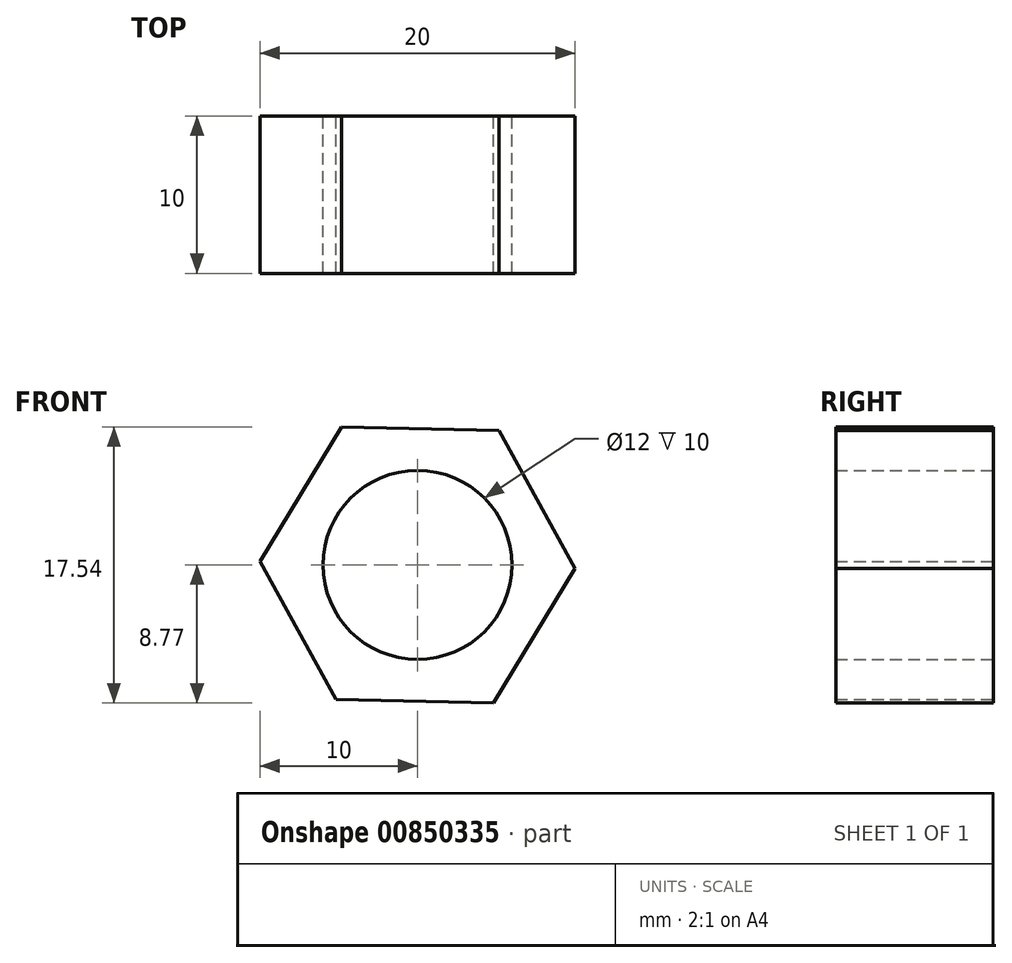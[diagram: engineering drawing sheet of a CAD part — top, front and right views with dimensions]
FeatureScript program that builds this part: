
annotation { "Feature Type Name" : "Feature", "Feature Type Description" : "" }
export const myFeature = defineFeature(function(context is Context, id is Id, definition is map)
    precondition{}
    {
        {
            var Q0;
            Q0=qCreatedBy(makeId("Front.planeOp"),FACE);
            var sketch = newSketch(context, id + "F0", { "sketchPlane" : qUnion([Q0])});
            skCircle(sketch, "E0.cCircle", {"center": v(0, 0) * mm, "radius": 8.66 * mm, "construction": true});
            skLineSegment(sketch, "E0.0", {"start": v(10, -0.21) * mm, "end": v(4.81, -8.77) * mm});
            skLineSegment(sketch, "E0.1", {"start": v(4.81, -8.77) * mm, "end": v(-5.18, -8.55) * mm});
            skLineSegment(sketch, "E0.2", {"start": v(-5.18, -8.55) * mm, "end": v(-10, 0.21) * mm});
            skLineSegment(sketch, "E0.3", {"start": v(-10, 0.21) * mm, "end": v(-4.81, 8.77) * mm});
            skLineSegment(sketch, "E0.4", {"start": v(-4.81, 8.77) * mm, "end": v(5.18, 8.55) * mm});
            skLineSegment(sketch, "E0.5", {"start": v(5.18, 8.55) * mm, "end": v(10, -0.21) * mm});
            skPoint(sketch, "E0.0.midPoint", {"position": v(7.4, -4.49) * mm});
            skCircle(sketch, "E1", {"center": v(0, 0) * mm, "radius": 6 * mm});
            skSolve(sketch);
        }
        {
            var Q0;
            Q0 = qSketchRegion(id + "F0", true);
            extrude(context, id + "F1", {"entities" : qUnion([Q0]), "depth" : 10 * mm, "offsetDistance" : 25 * mm});
        }
    });
